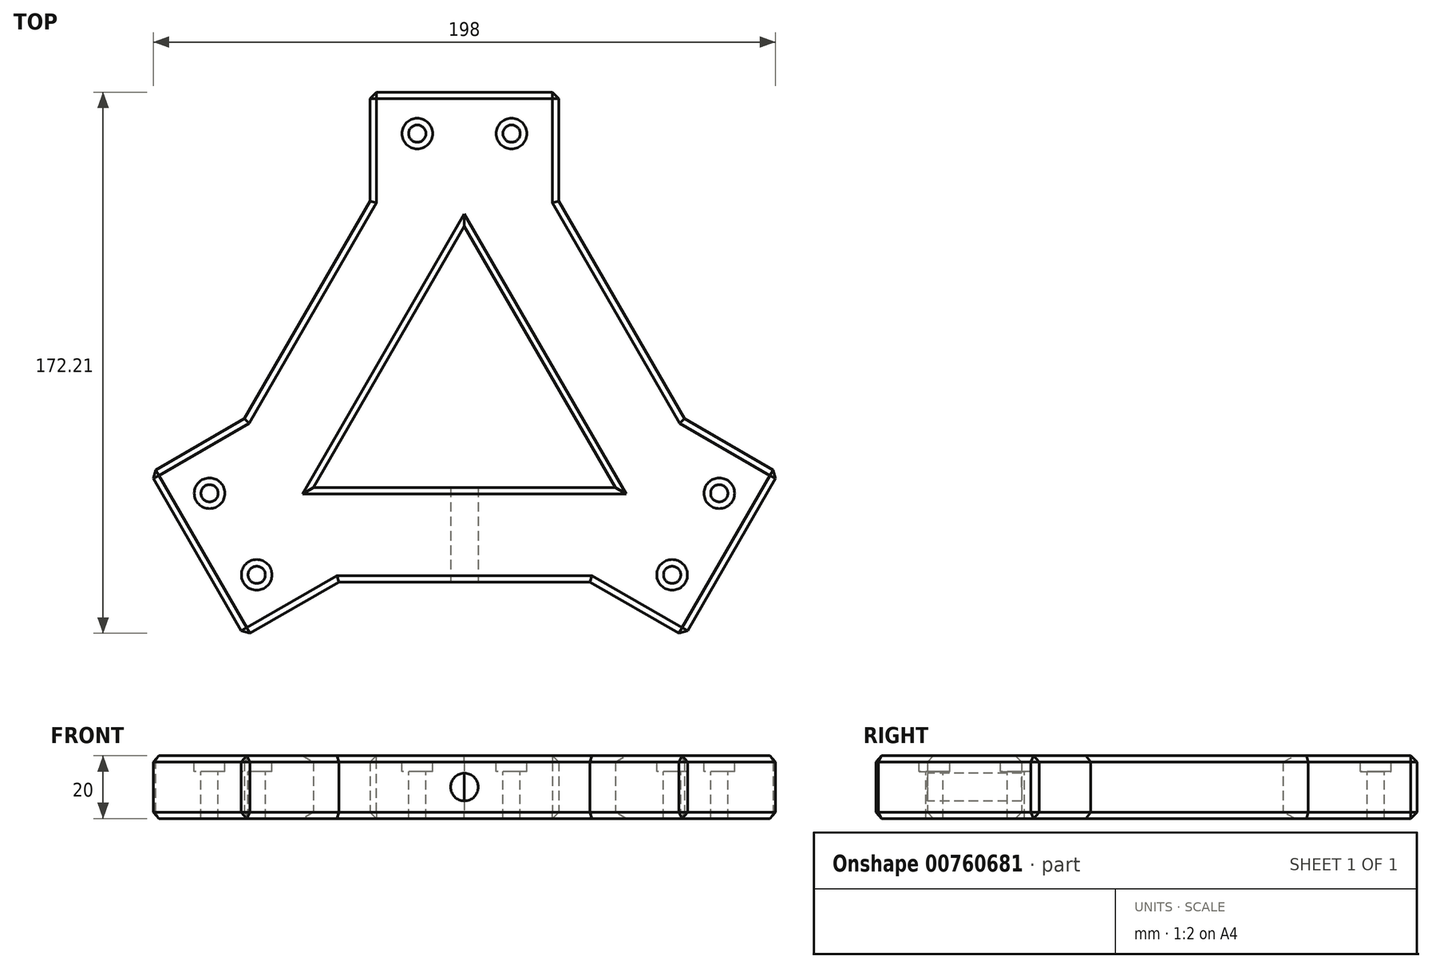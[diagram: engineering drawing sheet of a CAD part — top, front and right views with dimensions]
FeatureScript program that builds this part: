
annotation { "Feature Type Name" : "Feature", "Feature Type Description" : "" }
export const myFeature = defineFeature(function(context is Context, id is Id, definition is map)
    precondition{}
    {
        {
            var Q0;
            Q0=qCreatedBy(makeId("Top.planeOp"),FACE);
            var sketch = newSketch(context, id + "F0", { "sketchPlane" : qUnion([Q0])});
            skLineSegment(sketch, "E0", {"start": v(-100, -57.74) * mm, "end": v(100, -57.74) * mm});
            skLineSegment(sketch, "E1", {"start": v(100, -57.74) * mm, "end": v(0, 115.47) * mm});
            skLineSegment(sketch, "E2", {"start": v(0, 115.47) * mm, "end": v(-100, -57.74) * mm});
            skLineSegment(sketch, "E3", {"start": v(-100, -57.74) * mm, "end": v(50, 28.87) * mm, "construction": true});
            skLineSegment(sketch, "E4", {"start": v(0, 115.47) * mm, "end": v(0, -57.74) * mm, "construction": true});
            skPoint(sketch, "E5", {"position": v(0, 0) * mm});
            skLineSegment(sketch, "E6.0", {"start": v(0, 55.47) * mm, "end": v(-48.04, -27.74) * mm});
            skLineSegment(sketch, "E6.1", {"start": v(48.04, -27.74) * mm, "end": v(0, 55.47) * mm});
            skLineSegment(sketch, "E6.2", {"start": v(-48.04, -27.74) * mm, "end": v(48.04, -27.74) * mm});
            skSolve(sketch);
        }
        {
            var Q0;
            Q0=makeQuery(id+"F0.imprint","IMPRINT",FACE,{"disambiguationData":[TD([[makeQuery(id+"F0.imprint","IMPRINT",EDGE,{"derivedFrom":sQuery(id+"F0.wireOp",EDGE,"E0")}),1.0]])]});
            extrude(context, id + "F1", {"entities" : qUnion([Q0]), "depth" : 20 * mm, "offsetDistance" : 25 * mm});
        }
        {
            var Q0;
            Q0=makeQuery(id+"F1.opExtrude","SWEPT_EDGE",EDGE,{"disambiguationData":[OSD([sQuery(id+"F0.wireOp",EDGE,"E0"),sQuery(id+"F0.wireOp",EDGE,"E2")])]});
            var Q1;
            Q1=makeQuery(id+"F1.opExtrude","SWEPT_EDGE",EDGE,{"disambiguationData":[OSD([sQuery(id+"F0.wireOp",EDGE,"E0"),sQuery(id+"F0.wireOp",EDGE,"E1")])]});
            var Q2;
            Q2=makeQuery(id+"F1.opExtrude","SWEPT_EDGE",EDGE,{"disambiguationData":[OSD([sQuery(id+"F0.wireOp",EDGE,"E1"),sQuery(id+"F0.wireOp",EDGE,"E2")])]});
            chamfer(context, id + "F2", {"entities" : qUnion([Q0, Q1, Q2]), "width" : 20 * mm, "tangentPropagation" : true});
        }
        {
            var Q0;
            Q0=makeQuery(id+"F1.opExtrude","CAP_FACE",FACE,{"disambiguationData":[OSD([sQuery(id+"F0.wireOp",EDGE,"E0"),sQuery(id+"F0.wireOp",EDGE,"E1"),sQuery(id+"F0.wireOp",EDGE,"E2"),sQuery(id+"F0.wireOp",EDGE,"E6.0"),sQuery(id+"F0.wireOp",EDGE,"E6.1"),sQuery(id+"F0.wireOp",EDGE,"E6.2")])],"isStart":true});
            var sketch = newSketch(context, id + "F3", { "sketchPlane" : qUnion([Q0])});
            skLineSegment(sketch, "E7.bottom", {"start": v(-30, -98.15) * mm, "end": v(30, -98.15) * mm});
            skLineSegment(sketch, "E7.top", {"start": v(-30, -63.5) * mm, "end": v(30, -63.5) * mm});
            skLineSegment(sketch, "E7.left", {"start": v(-30, -98.15) * mm, "end": v(-30, -63.5) * mm});
            skLineSegment(sketch, "E7.right", {"start": v(30, -98.15) * mm, "end": v(30, -63.5) * mm});
            skLineSegment(sketch, "E8.1.0", {"start": v(100, 23.1) * mm, "end": v(70, 5.77) * mm});
            skLineSegment(sketch, "E8.1.1", {"start": v(70, 75.06) * mm, "end": v(40, 57.74) * mm});
            skLineSegment(sketch, "E8.1.2", {"start": v(70, 5.77) * mm, "end": v(40, 57.74) * mm});
            skLineSegment(sketch, "E8.1.3", {"start": v(100, 23.1) * mm, "end": v(70, 75.06) * mm});
            skLineSegment(sketch, "E8.2.0", {"start": v(-70, 75.06) * mm, "end": v(-40, 57.74) * mm});
            skLineSegment(sketch, "E8.2.1", {"start": v(-100, 23.1) * mm, "end": v(-70, 5.77) * mm});
            skLineSegment(sketch, "E8.2.2", {"start": v(-40, 57.74) * mm, "end": v(-70, 5.77) * mm});
            skLineSegment(sketch, "E8.2.3", {"start": v(-70, 75.06) * mm, "end": v(-100, 23.1) * mm});
            skPoint(sketch, "E8.center", {"position": v(0, 0) * mm});
            skSolve(sketch);
        }
        {
            var Q0;
            Q0 = qSketchRegion(id + "F3", true);
            var Q1;
            Q1=makeQuery(id+"F1.opExtrude","CAP_FACE",FACE,{"disambiguationData":[OSD([sQuery(id+"F0.wireOp",EDGE,"E0"),sQuery(id+"F0.wireOp",EDGE,"E1"),sQuery(id+"F0.wireOp",EDGE,"E2"),sQuery(id+"F0.wireOp",EDGE,"E6.0"),sQuery(id+"F0.wireOp",EDGE,"E6.1"),sQuery(id+"F0.wireOp",EDGE,"E6.2")])],"isStart":false});
            extrude(context, id + "F4", {"entities" : qUnion([Q0]), "operationType" : NewBodyOperationType.ADD, "endBound" : BoundingType.UP_TO_SURFACE, "oppositeDirection" : true, "depth" : 25 * mm, "endBoundEntityFace" : qUnion([Q1]), "offsetDistance" : 25 * mm});
        }
        {
            var Q0;
            {var subQ0=sQuery(id+"F0.wireOp",EDGE,"E6.2");var subQ1=sQuery(id+"F0.wireOp",EDGE,"E6.1");var subQ2=sQuery(id+"F0.wireOp",EDGE,"E6.0");var subQ3=sQuery(id+"F0.wireOp",EDGE,"E2");var subQ4=sQuery(id+"F0.wireOp",EDGE,"E1");var subQ5=sQuery(id+"F0.wireOp",EDGE,"E0");Q0=makeQuery(id+"F4.boolean.opBoolean","MERGE",FACE,{"derivedFrom":[makeQuery(id+"F1.opExtrude","CAP_FACE",FACE,{"disambiguationData":[OSD([subQ5,subQ4,subQ3,subQ2,subQ1,subQ0])],"isStart":false}),makeQuery(id+"F4.opExtrude","CAP_FACE",FACE,{"disambiguationData":[OSD([subQ5,subQ4,subQ3,subQ2,subQ1,subQ0]),OD(0.0)],"isStart":false}),makeQuery(id+"F4.opExtrude","CAP_FACE",FACE,{"disambiguationData":[OSD([subQ5,subQ4,subQ3,subQ2,subQ1,subQ0]),OD(1.0)],"isStart":false}),makeQuery(id+"F4.opExtrude","CAP_FACE",FACE,{"disambiguationData":[OSD([subQ5,subQ4,subQ3,subQ2,subQ1,subQ0]),OD(2.0)],"isStart":false})]});}
            var Q1;
            Q1=makeQuery(id+"F4.boolean.opBoolean","MERGE",FACE,{"derivedFrom":[makeQuery(id+"F1.opExtrude","CAP_FACE",FACE,{"disambiguationData":[OSD([sQuery(id+"F0.wireOp",EDGE,"E0"),sQuery(id+"F0.wireOp",EDGE,"E1"),sQuery(id+"F0.wireOp",EDGE,"E2"),sQuery(id+"F0.wireOp",EDGE,"E6.0"),sQuery(id+"F0.wireOp",EDGE,"E6.1"),sQuery(id+"F0.wireOp",EDGE,"E6.2")])],"isStart":true}),makeQuery(id+"F4.opExtrude","CAP_FACE",FACE,{"disambiguationData":[OSD([sQuery(id+"F3.wireOp",EDGE,"E7.bottom"),sQuery(id+"F3.wireOp",EDGE,"E7.top"),sQuery(id+"F3.wireOp",EDGE,"E7.left"),sQuery(id+"F3.wireOp",EDGE,"E7.right")])],"isStart":true}),makeQuery(id+"F4.opExtrude","CAP_FACE",FACE,{"disambiguationData":[OSD([sQuery(id+"F3.wireOp",EDGE,"E8.1.0"),sQuery(id+"F3.wireOp",EDGE,"E8.1.1"),sQuery(id+"F3.wireOp",EDGE,"E8.1.2"),sQuery(id+"F3.wireOp",EDGE,"E8.1.3")])],"isStart":true}),makeQuery(id+"F4.opExtrude","CAP_FACE",FACE,{"disambiguationData":[OSD([sQuery(id+"F3.wireOp",EDGE,"E8.2.0"),sQuery(id+"F3.wireOp",EDGE,"E8.2.1"),sQuery(id+"F3.wireOp",EDGE,"E8.2.2"),sQuery(id+"F3.wireOp",EDGE,"E8.2.3")])],"isStart":true})]});
            var Q2;
            Q2=makeQuery(id+"F4.opExtrude","SWEPT_EDGE",EDGE,{"disambiguationData":[OSD([sQuery(id+"F3.wireOp",EDGE,"E8.1.0"),sQuery(id+"F3.wireOp",EDGE,"E8.1.3")])]});
            var Q3;
            Q3=makeQuery(id+"F4.opExtrude","SWEPT_EDGE",EDGE,{"disambiguationData":[OSD([sQuery(id+"F3.wireOp",EDGE,"E8.1.1"),sQuery(id+"F3.wireOp",EDGE,"E8.1.3")])]});
            var Q4;
            Q4=makeQuery(id+"F4.opExtrude","SWEPT_EDGE",EDGE,{"disambiguationData":[OSD([sQuery(id+"F3.wireOp",EDGE,"E7.bottom"),sQuery(id+"F3.wireOp",EDGE,"E7.right")])]});
            var Q5;
            Q5=makeQuery(id+"F4.opExtrude","SWEPT_EDGE",EDGE,{"disambiguationData":[OSD([sQuery(id+"F3.wireOp",EDGE,"E7.bottom"),sQuery(id+"F3.wireOp",EDGE,"E7.left")])]});
            var Q6;
            Q6=makeQuery(id+"F4.opExtrude","SWEPT_EDGE",EDGE,{"disambiguationData":[OSD([sQuery(id+"F3.wireOp",EDGE,"E8.2.1"),sQuery(id+"F3.wireOp",EDGE,"E8.2.3")])]});
            var Q7;
            Q7=makeQuery(id+"F4.opExtrude","SWEPT_EDGE",EDGE,{"disambiguationData":[OSD([sQuery(id+"F3.wireOp",EDGE,"E8.2.0"),sQuery(id+"F3.wireOp",EDGE,"E8.2.3")])]});
            chamfer(context, id + "F5", {"entities" : qUnion([Q0, Q1, Q2, Q3, Q4, Q5, Q6, Q7]), "width" : 2 * mm, "tangentPropagation" : true});
        }
        {
            var Q0;
            {var subQ0=sQuery(id+"F0.wireOp",EDGE,"E6.2");var subQ1=sQuery(id+"F0.wireOp",EDGE,"E6.1");var subQ2=sQuery(id+"F0.wireOp",EDGE,"E6.0");var subQ3=sQuery(id+"F0.wireOp",EDGE,"E2");var subQ4=sQuery(id+"F0.wireOp",EDGE,"E1");var subQ5=sQuery(id+"F0.wireOp",EDGE,"E0");Q0=makeQuery(id+"F4.boolean.opBoolean","MERGE",FACE,{"derivedFrom":[makeQuery(id+"F1.opExtrude","CAP_FACE",FACE,{"disambiguationData":[OSD([subQ5,subQ4,subQ3,subQ2,subQ1,subQ0])],"isStart":false}),makeQuery(id+"F4.opExtrude","CAP_FACE",FACE,{"disambiguationData":[OSD([subQ5,subQ4,subQ3,subQ2,subQ1,subQ0]),OD(0.0)],"isStart":false}),makeQuery(id+"F4.opExtrude","CAP_FACE",FACE,{"disambiguationData":[OSD([subQ5,subQ4,subQ3,subQ2,subQ1,subQ0]),OD(1.0)],"isStart":false}),makeQuery(id+"F4.opExtrude","CAP_FACE",FACE,{"disambiguationData":[OSD([subQ5,subQ4,subQ3,subQ2,subQ1,subQ0]),OD(2.0)],"isStart":false})]});}
            var sketch = newSketch(context, id + "F6", { "sketchPlane" : qUnion([Q0])});
            skPoint(sketch, "E9", {"position": v(-15, 85) * mm});
            skPoint(sketch, "E10", {"position": v(15, 85) * mm});
            skLineSegment(sketch, "E11", {"start": v(-46.28, 85) * mm, "end": v(52.23, 85) * mm, "construction": true});
            skLineSegment(sketch, "E12.1.0", {"start": v(-50.47, -82.58) * mm, "end": v(-99.73, 2.73) * mm, "construction": true});
            skPoint(sketch, "E12.1.1", {"position": v(-66.11, -55.5) * mm});
            skPoint(sketch, "E12.1.2", {"position": v(-81.11, -29.5) * mm});
            skLineSegment(sketch, "E12.2.0", {"start": v(96.75, -2.42) * mm, "end": v(47.5, -87.73) * mm, "construction": true});
            skPoint(sketch, "E12.2.1", {"position": v(81.11, -29.5) * mm});
            skPoint(sketch, "E12.2.2", {"position": v(66.11, -55.5) * mm});
            skPoint(sketch, "E12.center", {"position": v(0, 0) * mm});
            skSolve(sketch);
        }
        {
            var Q0;
            Q0=sQuery(id+"F6.wireOp",VERTEX,"E12.1.1");
            var Q1;
            Q1=sQuery(id+"F6.wireOp",VERTEX,"E12.1.2");
            var Q2;
            Q2=sQuery(id+"F6.wireOp",VERTEX,"E9");
            var Q3;
            Q3=sQuery(id+"F6.wireOp",VERTEX,"E10");
            var Q4;
            Q4=sQuery(id+"F6.wireOp",VERTEX,"E12.2.1");
            var Q5;
            Q5=sQuery(id+"F6.wireOp",VERTEX,"E12.2.2");
            var Q6;
            Q6=makeQuery(id+"F1.opExtrude","SWEPT_BODY",BODY,{"disambiguationData":[OSD([sQuery(id+"F0.wireOp",EDGE,"E0"),sQuery(id+"F0.wireOp",EDGE,"E1"),sQuery(id+"F0.wireOp",EDGE,"E2"),sQuery(id+"F0.wireOp",EDGE,"E6.0"),sQuery(id+"F0.wireOp",EDGE,"E6.1"),sQuery(id+"F0.wireOp",EDGE,"E6.2")])]});
            hole(context, id + "F7", {"style" : HoleStyle.C_BORE, "endStyle" : HoleEndStyle.THROUGH, "holeDiameter" : 5.5 * mm, "cBoreDiameter" : 9.75 * mm, "cBoreDepth" : 5 * mm, "majorDiameter" : 5 * mm, "isTappedThrough" : true, "tappedDepth" : 12 * mm, "tapClearance" : 3, "locations" : qUnion([Q0, Q1, Q2, Q3, Q4, Q5]), "scope" : qUnion([Q6])});
        }
        {
            var Q0;
            Q0=makeQuery(id+"F1.opExtrude","SWEPT_FACE",FACE,{"disambiguationData":[OSD([sQuery(id+"F0.wireOp",EDGE,"E0")])]});
            var sketch = newSketch(context, id + "F8", { "sketchPlane" : qUnion([Q0])});
            skPoint(sketch, "E13", {"position": v(0, 10) * mm});
            skLineSegment(sketch, "E14", {"start": v(-60.25, 10) * mm, "end": v(76.94, 10) * mm, "construction": true});
            skSolve(sketch);
        }
        {
            var Q0;
            Q0=sQuery(id+"F8.wireOp",VERTEX,"E13");
            var Q1;
            Q1=makeQuery(id+"F1.opExtrude","SWEPT_BODY",BODY,{"disambiguationData":[OSD([sQuery(id+"F0.wireOp",EDGE,"E0"),sQuery(id+"F0.wireOp",EDGE,"E1"),sQuery(id+"F0.wireOp",EDGE,"E2"),sQuery(id+"F0.wireOp",EDGE,"E6.0"),sQuery(id+"F0.wireOp",EDGE,"E6.1"),sQuery(id+"F0.wireOp",EDGE,"E6.2")])]});
            hole(context, id + "F9", {"style" : HoleStyle.SIMPLE, "endStyle" : HoleEndStyle.BLIND, "standardTappedOrClearance" : lookupTablePath({ "standard" : "ISO", "engagement" : "75%", "pitch" : "1.25 mm", "size" : "M10", "type" : "Tapped" }), "standardBlindInLast" : lookupTablePath({ "standard" : "ISO", "engagement" : "75%", "pitch" : "1.25 mm", "size" : "M10", "type" : "Tapped" }), "holeDiameter" : 8.8 * mm, "majorDiameter" : 10 * mm, "showTappedDepth" : true, "holeDepth" : 51.35 * mm, "isTappedThrough" : true, "tappedDepth" : 47.6 * mm, "tapClearance" : 3, "locations" : qUnion([Q0]), "scope" : qUnion([Q1])});
        }
    });
